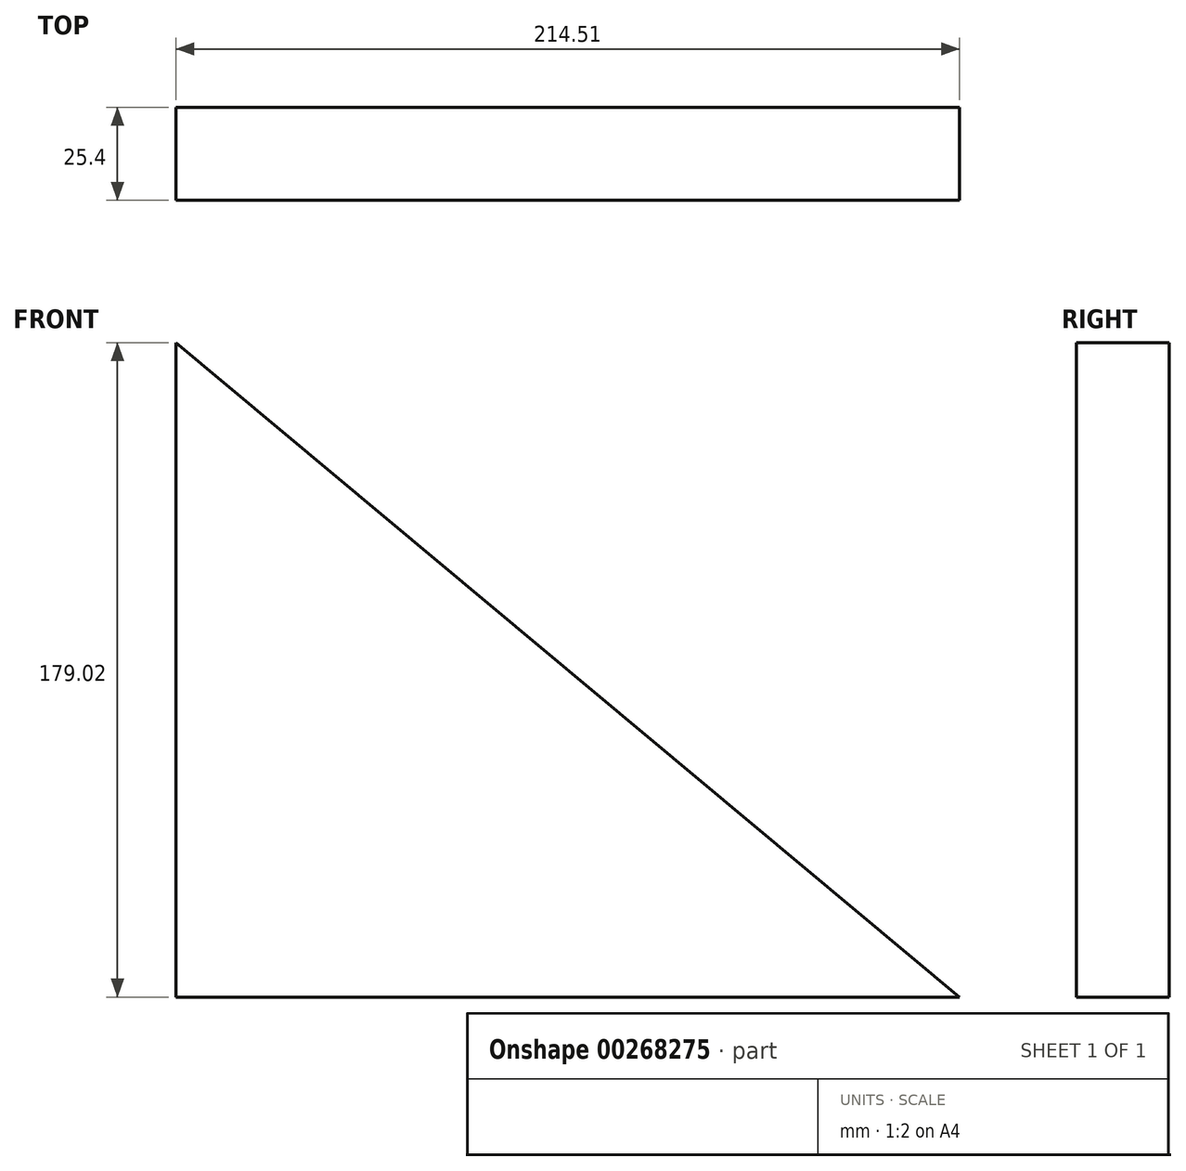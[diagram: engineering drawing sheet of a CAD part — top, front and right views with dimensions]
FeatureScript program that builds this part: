
annotation { "Feature Type Name" : "Feature", "Feature Type Description" : "" }
export const myFeature = defineFeature(function(context is Context, id is Id, definition is map)
    precondition{}
    {
        {
            var Q0;
            Q0=qCreatedBy(makeId("Front.planeOp"),FACE);
            var sketch = newSketch(context, id + "F0", { "sketchPlane" : qUnion([Q0])});
            skLineSegment(sketch, "E0", {"start": v(-114.02, 99.65) * mm, "end": v(-114.02, -79.37) * mm});
            skLineSegment(sketch, "E1", {"start": v(-114.02, -79.37) * mm, "end": v(100.49, -79.37) * mm});
            skLineSegment(sketch, "E2", {"start": v(100.49, -79.37) * mm, "end": v(-114.02, 99.65) * mm});
            skSolve(sketch);
        }
        {
            var Q0;
            Q0=makeQuery(id+"F0.imprint","IMPRINT",FACE,{"disambiguationData":[TD([[makeQuery(id+"F0.imprint","IMPRINT",EDGE,{"derivedFrom":sQuery(id+"F0.wireOp",EDGE,"E0")}),1.0]])]});
            extrude(context, id + "F1", {"entities" : qUnion([Q0]), "depth" : 25.4 * mm});
        }
    });
